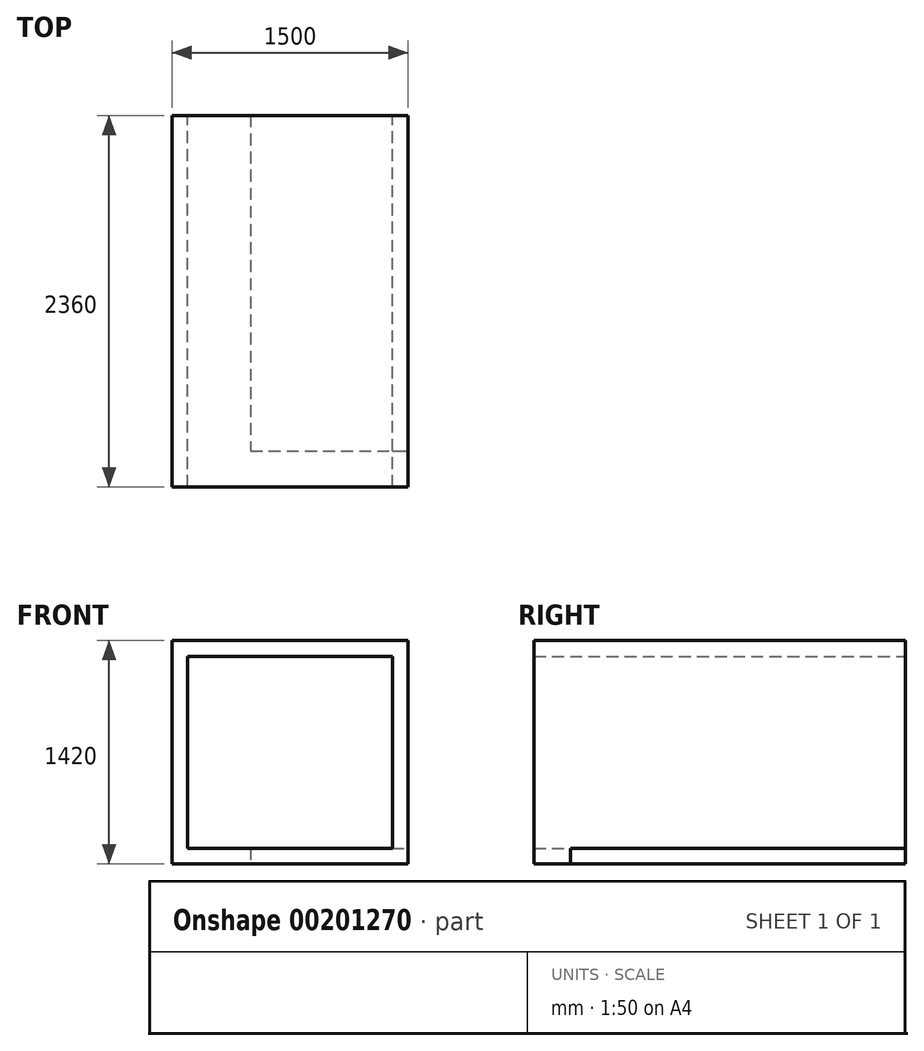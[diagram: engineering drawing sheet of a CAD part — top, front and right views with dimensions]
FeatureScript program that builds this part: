
annotation { "Feature Type Name" : "Feature", "Feature Type Description" : "" }
export const myFeature = defineFeature(function(context is Context, id is Id, definition is map)
    precondition{}
    {
        {
            var Q0;
            Q0=qCreatedBy(makeId("Front.planeOp"),FACE);
            var sketch = newSketch(context, id + "F1", { "sketchPlane" : qUnion([Q0])});
            skLineSegment(sketch, "E0.bottom", {"start": v(0, 0) * mm, "end": v(1300, 0) * mm});
            skLineSegment(sketch, "E0.top", {"start": v(0, 1220) * mm, "end": v(1300, 1220) * mm});
            skLineSegment(sketch, "E0.left", {"start": v(0, 0) * mm, "end": v(0, 1220) * mm});
            skLineSegment(sketch, "E0.right", {"start": v(1300, 0) * mm, "end": v(1300, 1220) * mm});
            skLineSegment(sketch, "E1.0", {"start": v(-100, -100) * mm, "end": v(-100, 1320) * mm});
            skLineSegment(sketch, "E1.1", {"start": v(-100, -100) * mm, "end": v(1400, -100) * mm});
            skLineSegment(sketch, "E1.2", {"start": v(1400, -100) * mm, "end": v(1400, 1320) * mm});
            skLineSegment(sketch, "E1.3", {"start": v(-100, 1320) * mm, "end": v(1400, 1320) * mm});
            skSolve(sketch);
        }
        {
            var Q0;
            Q0=makeQuery(id+"F1.imprint","IMPRINT",FACE,{"disambiguationData":[TD([[makeQuery(id+"F1.imprint","IMPRINT",EDGE,{"derivedFrom":sQuery(id+"F1.wireOp",EDGE,"E0.bottom")}),-1.0]])]});
            extrude(context, id + "F2", {"entities" : qUnion([Q0]), "depth" : 2360 * mm});
        }
        {
            var Q0;
            Q0=makeQuery(id+"F2.opExtrude","SWEPT_FACE",FACE,{"disambiguationData":[OSD([sQuery(id+"F1.wireOp",EDGE,"E1.1")])]});
            var sketch = newSketch(context, id + "F3", { "sketchPlane" : qUnion([Q0])});
            skLineSegment(sketch, "E2.bottom", {"start": v(400, 0) * mm, "end": v(1400, 0) * mm});
            skLineSegment(sketch, "E2.top", {"start": v(400, 2130) * mm, "end": v(1400, 2130) * mm});
            skLineSegment(sketch, "E2.left", {"start": v(400, 0) * mm, "end": v(400, 2130) * mm});
            skLineSegment(sketch, "E2.right", {"start": v(1400, 0) * mm, "end": v(1400, 2130) * mm});
            skSolve(sketch);
        }
        {
            var Q0;
            Q0 = qSketchRegion(id + "F3", true);
            extrude(context, id + "F0", {"entities" : qUnion([Q0]), "operationType" : NewBodyOperationType.REMOVE, "oppositeDirection" : true, "depth" : 100 * mm});
        }
    });
